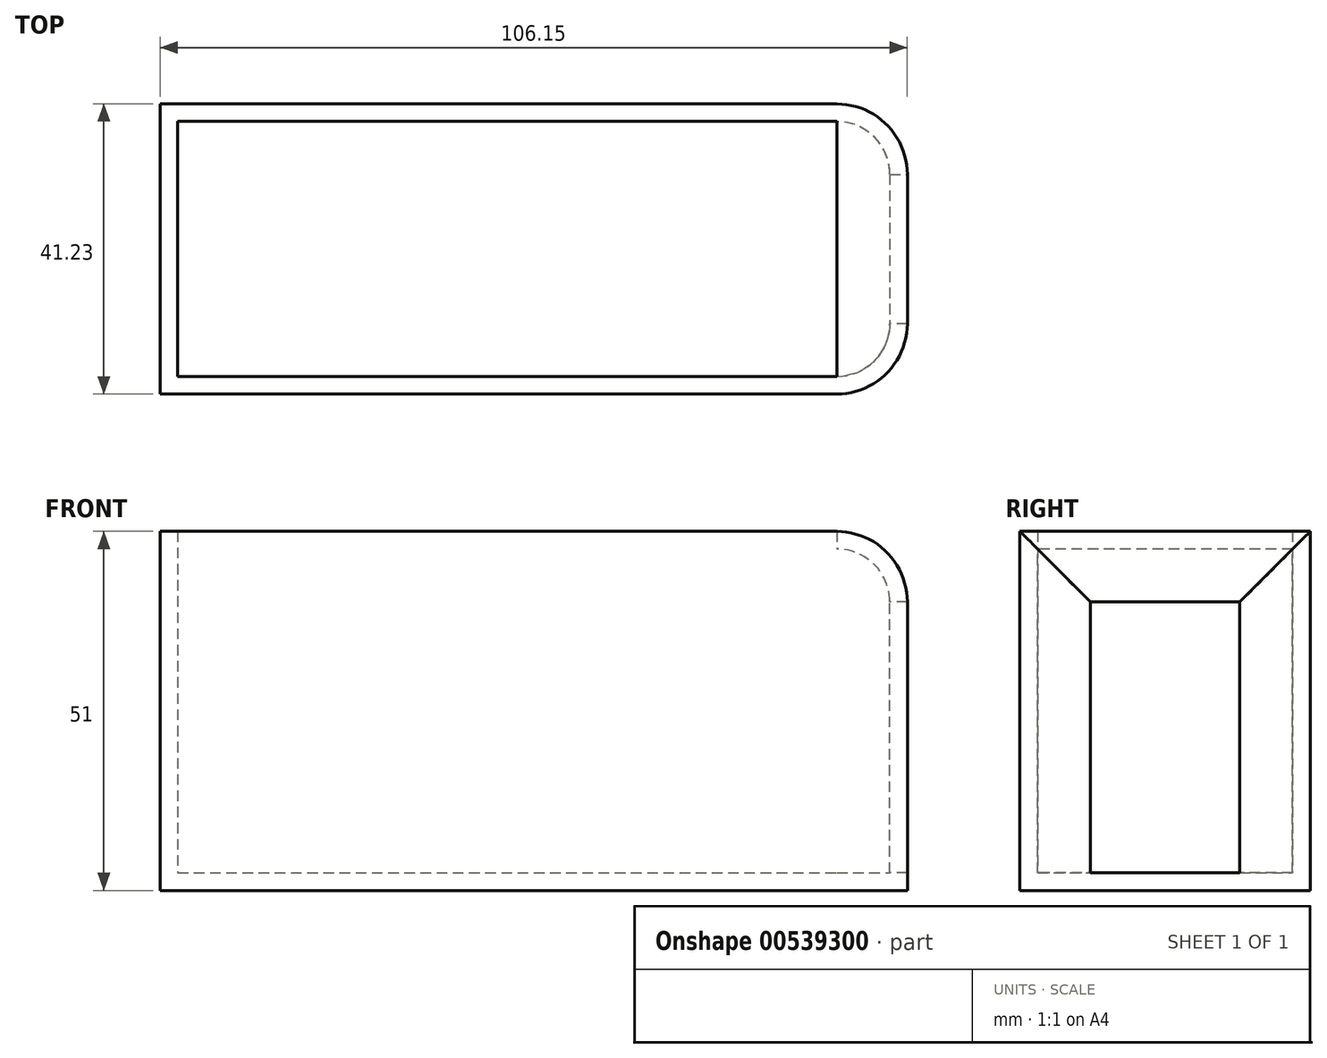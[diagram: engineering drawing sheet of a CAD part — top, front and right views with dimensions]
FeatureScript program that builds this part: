
annotation { "Feature Type Name" : "Feature", "Feature Type Description" : "" }
export const myFeature = defineFeature(function(context is Context, id is Id, definition is map)
    precondition{}
    {
        {
            var Q0;
            Q0=qCreatedBy(makeId("Top.planeOp"),FACE);
            var sketch = newSketch(context, id + "F0", { "sketchPlane" : qUnion([Q0])});
            skLineSegment(sketch, "E0.bottom", {"start": v(-50.62, -24.04) * mm, "end": v(55.53, -24.04) * mm});
            skLineSegment(sketch, "E0.top", {"start": v(-50.62, -65.27) * mm, "end": v(55.53, -65.27) * mm});
            skLineSegment(sketch, "E0.left", {"start": v(-50.62, -24.04) * mm, "end": v(-50.62, -65.27) * mm});
            skLineSegment(sketch, "E0.right", {"start": v(55.53, -24.04) * mm, "end": v(55.53, -65.27) * mm});
            skSolve(sketch);
        }
        {
            var Q0;
            Q0=makeQuery(id+"F0.imprint","IMPRINT",FACE,{"disambiguationData":[TD([[makeQuery(id+"F0.imprint","IMPRINT",EDGE,{"derivedFrom":sQuery(id+"F0.wireOp",EDGE,"E0.bottom")}),-1.0]])]});
            extrude(context, id + "F1", {"entities" : qUnion([Q0]), "depth" : 51 * mm, "offsetDistance" : 25 * mm});
        }
        {
            var Q0;
            Q0=makeQuery(id+"F1.opExtrude","SWEPT_EDGE",EDGE,{"disambiguationData":[OSD([sQuery(id+"F0.wireOp",EDGE,"E0.top"),sQuery(id+"F0.wireOp",EDGE,"E0.right")])]});
            var Q1;
            Q1=makeQuery(id+"F1.opExtrude","SWEPT_EDGE",EDGE,{"disambiguationData":[OSD([sQuery(id+"F0.wireOp",EDGE,"E0.bottom"),sQuery(id+"F0.wireOp",EDGE,"E0.right")])]});
            var Q2;
            Q2=makeQuery(id+"F1.opExtrude","CAP_EDGE",EDGE,{"disambiguationData":[OSD([sQuery(id+"F0.wireOp",EDGE,"E0.right")])],"isStart":false});
            fillet(context, id + "F2", {"entities" : qUnion([Q0, Q1, Q2]), "radius" : 10 * mm, "tangentPropagation" : true, "allowEdgeOverflow" : false});
        }
        {
            var Q0;
            Q0=makeQuery(id+"F1.opExtrude","CAP_FACE",FACE,{"disambiguationData":[OSD([sQuery(id+"F0.wireOp",EDGE,"E0.bottom"),sQuery(id+"F0.wireOp",EDGE,"E0.top"),sQuery(id+"F0.wireOp",EDGE,"E0.left"),sQuery(id+"F0.wireOp",EDGE,"E0.right")])],"isStart":false});
            var Q1;
            Q1=makeQuery(id+"F1.opExtrude","SWEPT_FACE",FACE,{"disambiguationData":[OSD([sQuery(id+"F0.wireOp",EDGE,"E0.right")])]});
            shell(context, id + "F3", {"entities" : qUnion([Q0, Q1]), "thickness" : 2.5 * mm});
        }
    });
